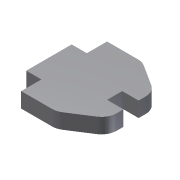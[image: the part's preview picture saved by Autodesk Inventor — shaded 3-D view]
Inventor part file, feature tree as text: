
AUTODESK INVENTOR PART (.ipt)
format: ipt  version: 2012 (Build 160160000, 160)  size: 95,744 bytes
history: native  units: mm
features: extrude x1, sketch x1
ambient origin geometry x8: Origin, YZ Plane, XZ Plane, XY Plane, X Axis, Y Axis, Z Axis, Center Point
bodies: Solid1 (feature_tree)
feature tree (2):
  extrude  "Extrusion1"  Depth=3.0mm
  sketch  "Sketch1"  dims[d10=3.0mm d11=0.0mm d13=3.0mm d26=7.0mm d27=9.0mm d28=4.0mm d29=4.0mm d30=7.0mm d33=4.5mm d34=3.0mm d35=1.5mm d36=3.0mm d37=3.0mm d38=3.0mm d39=3.0mm]
